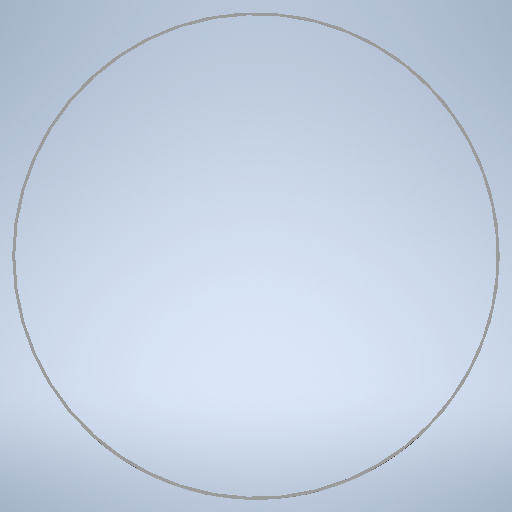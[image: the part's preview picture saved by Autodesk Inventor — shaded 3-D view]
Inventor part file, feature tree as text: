
AUTODESK INVENTOR PART (.ipt)
format: ipt  version: 2025.1 (Build 291241020, 241B)  size: 1,412,096 bytes
history: native  units: mm
features: other x9, sketch x6, extrude x4, revolve x1, plane x1
ambient origin geometry x8: Origin, YZ Plane, XZ Plane, XY Plane, X Axis, Y Axis, Z Axis, Center Point
bodies: Solid1 (feature_tree)
feature tree (21):
  revolve  "Revolution1"  [1 undecoded]
  extrude  "Extrusion1"  Depth=62.8144mm
  other  "floor angle sketch"
  other  "Feeder Plane"
  other  "Feeder horisont hight angle"
  other  "Feeder Work Plane"
  extrude  "Feeder Extrusion"  TaperAngle=0.0deg  [1 undecoded]
  other  "Inner Plane"
  other  "Inner horisont hight angle"
  other  "Inner Work Plane"
  extrude  "Inner Extrusion"  Depth=400.0mm
  other  "Outer Plane"
  sketch  "Sketch11"  dims[d16=400.0mm d17=180.0mm]
  plane  "Work Plane9"
  extrude  "Extrusion6"  Depth=400.0mm
  sketch  "Sketch1"  dims[d0=6.0mm d1=1900.0mm]
  sketch  "Sketch2"  dims[d2=960.0mm d3=62.8144mm]
  sketch  "Sketch8"  dims[d4=530.0mm d10=0.0mm d11=0.0mm]
  sketch  "Sketch10"  dims[d12=400.0mm d15=200.0mm]
  sketch  "Sketch12"  dims[d34=1500.0mm d35=30.0deg d36=172.0mm d38=10.0mm d39=0.0mm d40=0.0mm d41=1300.0mm d42=91.0mm d43=0.0mm d44=0.0mm d45=0.0mm d46=700.0mm d47=92.0mm d48=10.0mm d49=0.0mm]
  other  "Definition1"
note: 2 required parameter values undecoded (feature->parameter linkage not recoverable at this tier; creation-order binding heuristic only, values carry confidence <= 0.55)